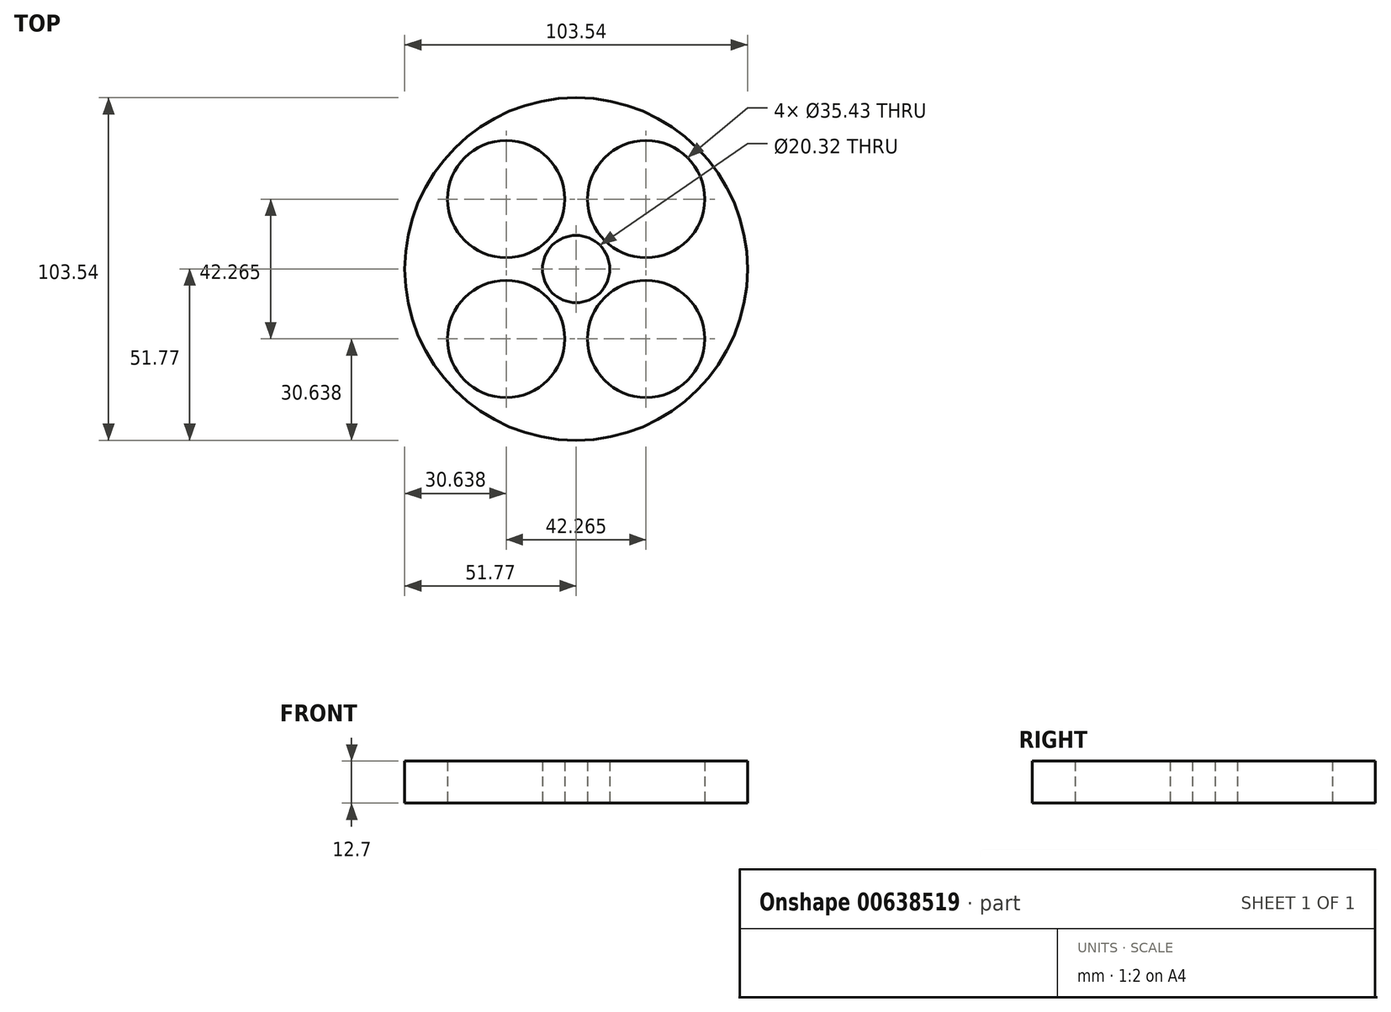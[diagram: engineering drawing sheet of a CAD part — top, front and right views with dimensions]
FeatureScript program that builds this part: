
annotation { "Feature Type Name" : "Feature", "Feature Type Description" : "" }
export const myFeature = defineFeature(function(context is Context, id is Id, definition is map)
    precondition{}
    {
        {
            var Q0;
            Q0=qCreatedBy(makeId("Top.planeOp"),FACE);
            var sketch = newSketch(context, id + "F0", { "sketchPlane" : qUnion([Q0])});
            skCircle(sketch, "E0", {"center": v(0, 0) * mm, "radius": 51.77 * mm});
            skCircle(sketch, "E1", {"center": v(0, 0) * mm, "radius": 10.16 * mm});
            skCircle(sketch, "E2", {"center": v(21.13, 21.13) * mm, "radius": 17.71 * mm});
            skCircle(sketch, "E3.MirrorC", {"center": v(-21.13, 21.13) * mm, "radius": 17.71 * mm});
            skCircle(sketch, "E4.MirrorC", {"center": v(21.13, -21.13) * mm, "radius": 17.71 * mm});
            skCircle(sketch, "E5.MirrorC", {"center": v(-21.13, -21.13) * mm, "radius": 17.71 * mm});
            skSolve(sketch);
        }
        {
            var Q0;
            Q0=makeQuery(id+"F0.imprint","IMPRINT",FACE,{"disambiguationData":[TD([[makeQuery(id+"F0.imprint","IMPRINT",EDGE,{"derivedFrom":sQuery(id+"F0.wireOp",EDGE,"E0")}),1.0]])]});
            extrude(context, id + "F1", {"entities" : qUnion([Q0]), "depth" : 12.7 * mm, "offsetDistance" : 25.4 * mm});
        }
    });
